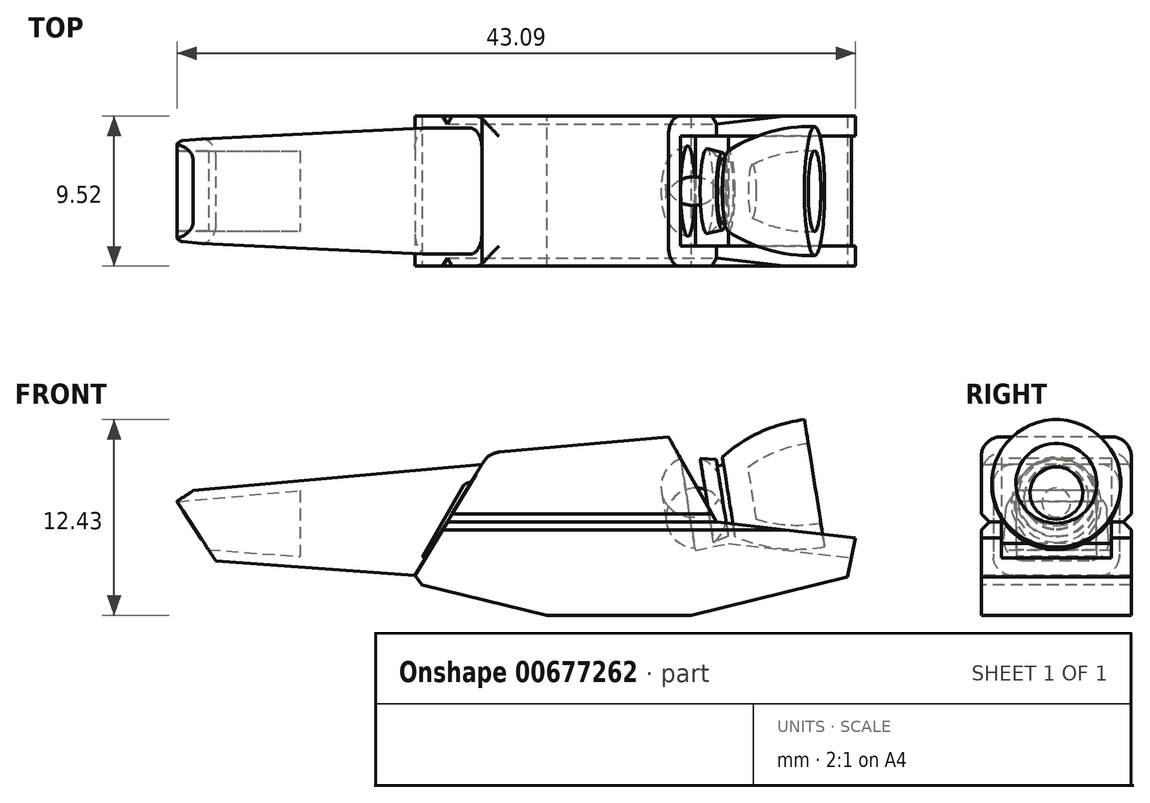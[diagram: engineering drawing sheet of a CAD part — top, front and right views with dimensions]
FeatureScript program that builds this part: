
annotation { "Feature Type Name" : "Feature", "Feature Type Description" : "" }
export const myFeature = defineFeature(function(context is Context, id is Id, definition is map)
    precondition{}
    {
        {
            var Q0;
            Q0=qCreatedBy(makeId("Front.planeOp"),FACE);
            var sketch = newSketch(context, id + "F0", { "sketchPlane" : qUnion([Q0])});
            skLineSegment(sketch, "E0", {"start": v(0, 0) * mm, "end": v(1.5, 0.24) * mm, "construction": true});
            skLineSegment(sketch, "E1", {"start": v(0, 0) * mm, "end": v(-2.23, 14.05) * mm, "construction": true});
            skLineSegment(sketch, "E2", {"start": v(5.05, 3.4) * mm, "end": v(4.82, 4.9) * mm});
            skLineSegment(sketch, "E3", {"start": v(-0.32, 2.02) * mm, "end": v(-0.4, 2.53) * mm});
            skArc(sketch, "E4", {"start": v(4.82, 4.9) * mm, "mid": v(2.02, 4.12) * mm, "end": v(-0.4, 2.53) * mm});
            skLineSegment(sketch, "E5", {"start": v(0, 0) * mm, "end": v(-19.66, -3.11) * mm, "construction": true});
            skLineSegment(sketch, "E6", {"start": v(-0.32, 2.02) * mm, "end": v(-0.72, 1.96) * mm});
            skLineSegment(sketch, "E7", {"start": v(-0.72, 1.96) * mm, "end": v(-0.79, 2.36) * mm});
            skLineSegment(sketch, "E8", {"start": v(-0.79, 2.36) * mm, "end": v(-1.8, 2.45) * mm});
            skLineSegment(sketch, "E9", {"start": v(-0.79, 2.36) * mm, "end": v(-6.83, 1.4) * mm, "construction": true});
            skLineSegment(sketch, "E10", {"start": v(-3.63, 6.1) * mm, "end": v(-2.98, 2.02) * mm, "construction": true});
            skLineSegment(sketch, "E11", {"start": v(-1.8, 2.45) * mm, "end": v(-3.02, 2.26) * mm, "construction": true});
            skPoint(sketch, "E12", {"position": v(-3.05, 2.42) * mm});
            skArc(sketch, "E13", {"start": v(-1.8, 2.45) * mm, "mid": v(-2.43, 2.54) * mm, "end": v(-3.05, 2.42) * mm});
            skLineSegment(sketch, "E14", {"start": v(-3.05, 2.42) * mm, "end": v(-2.6, -0.41) * mm});
            skLineSegment(sketch, "E15", {"start": v(-2.6, -0.41) * mm, "end": v(1.5, 0.24) * mm});
            skArc(sketch, "E16", {"start": v(5.05, 3.4) * mm, "mid": v(3.05, 2.9) * mm, "end": v(1.24, 1.9) * mm});
            skLineSegment(sketch, "E17", {"start": v(1.24, 1.9) * mm, "end": v(1.5, 0.24) * mm});
            skLineSegment(sketch, "E18.trimOffspring", {"start": v(5.46, 0.86) * mm, "end": v(24.57, 3.9) * mm, "construction": true});
            skSolve(sketch);
        }
        {
            var Q0;
            Q0=makeQuery(id+"F0.imprint","IMPRINT",FACE,{"disambiguationData":[TD([[makeQuery(id+"F0.imprint","IMPRINT",EDGE,{"derivedFrom":sQuery(id+"F0.wireOp",EDGE,"E2")}),1.0]])]});
            var Q1;
            Q1=sQuery(id+"F0.wireOp",EDGE,"E5");
            revolve(context, id + "F1", {"entities" : qUnion([Q0]), "axis" : qUnion([Q1]), "revolveType" : RevolveType.FULL});
        }
        {
            var Q0;
            Q0=qCreatedBy(makeId("Front.planeOp"),FACE);
            var sketch = newSketch(context, id + "F2", { "sketchPlane" : qUnion([Q0])});
            skLineSegment(sketch, "E19", {"start": v(0, 0) * mm, "end": v(1.56, -9.86) * mm, "construction": true});
            skLineSegment(sketch, "E20", {"start": v(0.48, -3.01) * mm, "end": v(7.8, -3.87) * mm});
            skLineSegment(sketch, "E21", {"start": v(7.8, -3.87) * mm, "end": v(7.55, -5.07) * mm});
            skLineSegment(sketch, "E22", {"start": v(7.55, -5.07) * mm, "end": v(-2.39, -7.52) * mm});
            skLineSegment(sketch, "E23", {"start": v(-2.39, -7.52) * mm, "end": v(-14.3, -6.85) * mm});
            skLineSegment(sketch, "E24", {"start": v(-19.92, -5) * mm, "end": v(-32.58, -4.06) * mm});
            skLineSegment(sketch, "E25", {"start": v(-35.04, -0.28) * mm, "end": v(-32.58, -4.06) * mm});
            skLineSegment(sketch, "E26", {"start": v(-34.01, 0.4) * mm, "end": v(-35.04, -0.28) * mm});
            skLineSegment(sketch, "E27", {"start": v(-34.01, 0.4) * mm, "end": v(-15.66, 2.07) * mm});
            skLineSegment(sketch, "E28", {"start": v(-15.66, 2.07) * mm, "end": v(-15.25, 2.78) * mm});
            skLineSegment(sketch, "E29", {"start": v(-15.25, 2.78) * mm, "end": v(-3.83, 3.82) * mm});
            skLineSegment(sketch, "E30", {"start": v(0.48, -3.01) * mm, "end": v(0, -2.95) * mm});
            skLineSegment(sketch, "E31", {"start": v(-3.83, 3.82) * mm, "end": v(-3.05, 2.44) * mm});
            skLineSegment(sketch, "E32", {"start": v(0, -2.95) * mm, "end": v(-50.8, -2.95) * mm, "construction": true});
            skLineSegment(sketch, "E33", {"start": v(-19.92, -5) * mm, "end": v(-19.48, -5.6) * mm});
            skLineSegment(sketch, "E34", {"start": v(-19.48, -5.6) * mm, "end": v(-14.3, -6.85) * mm});
            skLineSegment(sketch, "E35", {"start": v(-3.05, 2.44) * mm, "end": v(-2.12, -3.4) * mm});
            skLineSegment(sketch, "E36", {"start": v(-2.12, -3.4) * mm, "end": v(0, -2.95) * mm});
            skLineSegment(sketch, "E37", {"start": v(-2.12, -3.4) * mm, "end": v(-2.12, 15.55) * mm, "construction": true});
            skSolve(sketch);
        }
        {
            var Q0;
            Q0 = qSketchRegion(id + "F2", true);
            extrude(context, id + "F3", {"entities" : qUnion([Q0]), "operationType" : NewBodyOperationType.ADD, "endBound" : BoundingType.SYMMETRIC, "oppositeDirection" : true, "depth" : 9.52 * mm, "offsetDistance" : 25.4 * mm});
        }
        {
            var Q0;
            Q0=makeQuery(id+"F3.opExtrude","CAP_FACE",FACE,{"disambiguationData":[OSD([sQuery(id+"F2.wireOp",EDGE,"E20"),sQuery(id+"F2.wireOp",EDGE,"E21"),sQuery(id+"F2.wireOp",EDGE,"E22"),sQuery(id+"F2.wireOp",EDGE,"E23"),sQuery(id+"F2.wireOp",EDGE,"E24"),sQuery(id+"F2.wireOp",EDGE,"E25"),sQuery(id+"F2.wireOp",EDGE,"E26"),sQuery(id+"F2.wireOp",EDGE,"E27"),sQuery(id+"F2.wireOp",EDGE,"E28"),sQuery(id+"F2.wireOp",EDGE,"E29"),sQuery(id+"F2.wireOp",EDGE,"E30"),sQuery(id+"F2.wireOp",EDGE,"E31"),sQuery(id+"F2.wireOp",EDGE,"E33"),sQuery(id+"F2.wireOp",EDGE,"E34"),sQuery(id+"F2.wireOp",EDGE,"E35"),sQuery(id+"F2.wireOp",EDGE,"E36")])],"isStart":true});
            var sketch = newSketch(context, id + "F4", { "sketchPlane" : qUnion([Q0])});
            skLineSegment(sketch, "E38", {"start": v(7.8, -3.87) * mm, "end": v(8.05, -2.62) * mm});
            skLineSegment(sketch, "E39", {"start": v(8.05, -2.62) * mm, "end": v(-0.77, -1.59) * mm});
            skLineSegment(sketch, "E40", {"start": v(-3.05, 2.44) * mm, "end": v(-2.12, -3.4) * mm});
            skLineSegment(sketch, "E41", {"start": v(-2.12, -3.4) * mm, "end": v(0, -2.95) * mm});
            skLineSegment(sketch, "E42", {"start": v(0, -2.95) * mm, "end": v(7.8, -3.87) * mm});
            skLineSegment(sketch, "E43", {"start": v(-3.05, 2.44) * mm, "end": v(0, -2.95) * mm, "construction": true});
            skLineSegment(sketch, "E44", {"start": v(-3.05, 2.44) * mm, "end": v(-0.77, -1.59) * mm});
            skSolve(sketch);
        }
        {
            var Q0;
            Q0 = qSketchRegion(id + "F4", true);
            extrude(context, id + "F5", {"entities" : qUnion([Q0]), "oppositeDirection" : true, "depth" : 1.27 * mm, "offsetDistance" : 25.4 * mm});
        }
        {
            var Q0;
            Q0=makeQuery(id+"FYjz2R2zgnsnYFL_2.boolean.opBoolean","MERGE",FACE,{"derivedFrom":[makeQuery(id+"F3.opExtrude","CAP_FACE",FACE,{"disambiguationData":[OSD([sQuery(id+"F2.wireOp",EDGE,"E20"),sQuery(id+"F2.wireOp",EDGE,"E21"),sQuery(id+"F2.wireOp",EDGE,"E22"),sQuery(id+"F2.wireOp",EDGE,"E23"),sQuery(id+"F2.wireOp",EDGE,"E24"),sQuery(id+"F2.wireOp",EDGE,"E25"),sQuery(id+"F2.wireOp",EDGE,"E26"),sQuery(id+"F2.wireOp",EDGE,"E27"),sQuery(id+"F2.wireOp",EDGE,"E28"),sQuery(id+"F2.wireOp",EDGE,"E29"),sQuery(id+"F2.wireOp",EDGE,"E30"),sQuery(id+"F2.wireOp",EDGE,"E31"),sQuery(id+"F2.wireOp",EDGE,"E33"),sQuery(id+"F2.wireOp",EDGE,"E34"),sQuery(id+"F2.wireOp",EDGE,"E35"),sQuery(id+"F2.wireOp",EDGE,"E36")])],"isStart":true}),makeQuery(id+"F5.opExtrude","CAP_FACE",FACE,{"disambiguationData":[OSD([sQuery(id+"F4.wireOp",EDGE,"E38"),sQuery(id+"F4.wireOp",EDGE,"E39"),sQuery(id+"F4.wireOp",EDGE,"E40"),sQuery(id+"F4.wireOp",EDGE,"E41"),sQuery(id+"F4.wireOp",EDGE,"E42"),sQuery(id+"F4.wireOp",EDGE,"E44")])],"isStart":true})]});
            var sketch = newSketch(context, id + "F6", { "sketchPlane" : qUnion([Q0])});
            skLineSegment(sketch, "E45", {"start": v(-36.57, -5) * mm, "end": v(-36.57, 2.78) * mm});
            skLineSegment(sketch, "E46", {"start": v(-36.57, 2.78) * mm, "end": v(-15.25, 2.78) * mm});
            skLineSegment(sketch, "E47", {"start": v(-15.25, 2.78) * mm, "end": v(-19.92, -5) * mm});
            skLineSegment(sketch, "E48", {"start": v(-19.92, -5) * mm, "end": v(-36.57, -5) * mm});
            skSolve(sketch);
        }
        {
            var Q0;
            Q0 = qSketchRegion(id + "F6", true);
            extrude(context, id + "F7", {"entities" : qUnion([Q0]), "operationType" : NewBodyOperationType.REMOVE, "oppositeDirection" : true, "depth" : 0.76 * mm, "offsetDistance" : 25.4 * mm});
        }
        {
            var Q0;
            Q0=makeQuery(id+"F5.opExtrude","SWEPT_BODY",BODY,{"disambiguationData":[OSD([sQuery(id+"F4.wireOp",EDGE,"E38"),sQuery(id+"F4.wireOp",EDGE,"E39"),sQuery(id+"F4.wireOp",EDGE,"E40"),sQuery(id+"F4.wireOp",EDGE,"E41"),sQuery(id+"F4.wireOp",EDGE,"E42"),sQuery(id+"F4.wireOp",EDGE,"E44")])]});
            var Q1;
            Q1=qCreatedBy(makeId("Front.planeOp"),FACE);
            mirror(context, id + "F8", {"operationType" : NewBodyOperationType.ADD, "entities" : qUnion([Q0]), "mirrorPlane" : qUnion([Q1])});
        }
        {
            var Q0;
            Q0=makeQuery(id+"F8.boolean.opBoolean","MERGE",FACE,{"derivedFrom":[makeQuery(id+"F3.opExtrude","CAP_FACE",FACE,{"disambiguationData":[OSD([sQuery(id+"F2.wireOp",EDGE,"E20"),sQuery(id+"F2.wireOp",EDGE,"E21"),sQuery(id+"F2.wireOp",EDGE,"E22"),sQuery(id+"F2.wireOp",EDGE,"E23"),sQuery(id+"F2.wireOp",EDGE,"E24"),sQuery(id+"F2.wireOp",EDGE,"E25"),sQuery(id+"F2.wireOp",EDGE,"E26"),sQuery(id+"F2.wireOp",EDGE,"E27"),sQuery(id+"F2.wireOp",EDGE,"E28"),sQuery(id+"F2.wireOp",EDGE,"E29"),sQuery(id+"F2.wireOp",EDGE,"E30"),sQuery(id+"F2.wireOp",EDGE,"E31"),sQuery(id+"F2.wireOp",EDGE,"E33"),sQuery(id+"F2.wireOp",EDGE,"E34"),sQuery(id+"F2.wireOp",EDGE,"E35"),sQuery(id+"F2.wireOp",EDGE,"E36")])],"isStart":false}),makeQuery(id+"F8.opPattern","COPY",FACE,{"derivedFrom":makeQuery(id+"F5.opExtrude","CAP_FACE",FACE,{"disambiguationData":[OSD([sQuery(id+"F4.wireOp",EDGE,"E38"),sQuery(id+"F4.wireOp",EDGE,"E39"),sQuery(id+"F4.wireOp",EDGE,"E40"),sQuery(id+"F4.wireOp",EDGE,"E41"),sQuery(id+"F4.wireOp",EDGE,"E42"),sQuery(id+"F4.wireOp",EDGE,"E44")])],"isStart":true}),"instanceName":"1"})]});
            var sketch = newSketch(context, id + "F9", { "sketchPlane" : qUnion([Q0])});
            skLineSegment(sketch, "E49", {"start": v(15.25, 2.78) * mm, "end": v(19.92, -5) * mm});
            skLineSegment(sketch, "E50", {"start": v(19.92, -5) * mm, "end": v(36.16, -5) * mm});
            skLineSegment(sketch, "E51", {"start": v(36.16, -5) * mm, "end": v(36.16, 2.59) * mm});
            skLineSegment(sketch, "E52", {"start": v(36.16, 2.59) * mm, "end": v(15.25, 2.78) * mm});
            skSolve(sketch);
        }
        {
            var Q0;
            Q0 = qSketchRegion(id + "F9", true);
            extrude(context, id + "F10", {"entities" : qUnion([Q0]), "operationType" : NewBodyOperationType.REMOVE, "oppositeDirection" : true, "depth" : 0.76 * mm, "offsetDistance" : 25.4 * mm});
        }
        {
            var Q0;
            Q0=makeQuery(id+"F3.opExtrude","SWEPT_EDGE",EDGE,{"disambiguationData":[OSD([sQuery(id+"F2.wireOp",EDGE,"E27"),sQuery(id+"F2.wireOp",EDGE,"E28")])]});
            var Q1;
            Q1=makeQuery(id+"F3.opExtrude","SWEPT_FACE",FACE,{"disambiguationData":[OSD([sQuery(id+"F2.wireOp",EDGE,"E28")])]});
            cPlane(context, id + "F11", {"entities" : qUnion([Q0, Q1]), "cplaneType" : CPlaneType.LINE_ANGLE, "offset" : 25.4 * mm, "angle" : 90 * degree, "width" : 152.4 * mm, "height" : 152.4 * mm});
        }
        {
            var Q0;
            Q0=qCreatedBy(id+"F11.planeOp",FACE);
            var sketch = newSketch(context, id + "F12", { "sketchPlane" : qUnion([Q0])});
            skLineSegment(sketch, "E53", {"start": v(-14.89, -7.16) * mm, "end": v(-14.89, 7.16) * mm, "construction": true});
            skLineSegment(sketch, "E54", {"start": v(0, 0) * mm, "end": v(-46.94, 0) * mm, "construction": true});
            skLineSegment(sketch, "E55", {"start": v(-30.26, -3.18) * mm, "end": v(-30.26, 3.18) * mm, "construction": true});
            skLineSegment(sketch, "E56", {"start": v(-30.26, -3.18) * mm, "end": v(-14.89, -4) * mm});
            skLineSegment(sketch, "E57", {"start": v(-14.89, -4) * mm, "end": v(-30.26, -4.28) * mm});
            skLineSegment(sketch, "E58", {"start": v(-30.26, -4.28) * mm, "end": v(-30.26, -3.18) * mm});
            skLineSegment(sketch, "E59.MirrorCS", {"start": v(-14.89, 4) * mm, "end": v(-30.26, 4.28) * mm});
            skLineSegment(sketch, "E60.MirrorCS", {"start": v(-30.26, 3.18) * mm, "end": v(-14.89, 4) * mm});
            skLineSegment(sketch, "E61.MirrorCS", {"start": v(-30.26, 4.28) * mm, "end": v(-30.26, 3.18) * mm});
            skSolve(sketch);
        }
        {
            var Q0;
            Q0 = qSketchRegion(id + "F12", true);
            extrude(context, id + "F13", {"entities" : qUnion([Q0]), "operationType" : NewBodyOperationType.REMOVE, "endBound" : BoundingType.THROUGH_ALL, "oppositeDirection" : true, "depth" : 25.4 * mm, "offsetDistance" : 25.4 * mm});
        }
        {
            var Q0;
            Q0=qCreatedBy(makeId("Front.planeOp"),FACE);
            var sketch = newSketch(context, id + "F14", { "sketchPlane" : qUnion([Q0])});
            skLineSegment(sketch, "E62", {"start": v(-35.68, -0.37) * mm, "end": v(-27.21, 0.4) * mm});
            skLineSegment(sketch, "E63", {"start": v(0.5, 0) * mm, "end": v(-37.1, 0) * mm, "construction": true});
            skLineSegment(sketch, "E64", {"start": v(-33.95, -3.29) * mm, "end": v(-27.21, -3.79) * mm});
            skLineSegment(sketch, "E65", {"start": v(-33.95, -3.29) * mm, "end": v(-35.68, -0.37) * mm});
            skLineSegment(sketch, "E66", {"start": v(-27.21, 0.4) * mm, "end": v(-27.21, -3.79) * mm});
            skPoint(sketch, "E67.orphan", {"position": v(-19.1, 1.14) * mm});
            skSolve(sketch);
        }
        {
            var Q0;
            Q0 = qSketchRegion(id + "F14", true);
            extrude(context, id + "F15", {"entities" : qUnion([Q0]), "operationType" : NewBodyOperationType.REMOVE, "endBound" : BoundingType.SYMMETRIC, "oppositeDirection" : true, "depth" : 5.08 * mm, "offsetDistance" : 25.4 * mm});
        }
        {
            var Q0;
            Q0=qCreatedBy(makeId("Right.planeOp"),FACE);
            var sketch = newSketch(context, id + "F16", { "sketchPlane" : qUnion([Q0])});
            skLineSegment(sketch, "E68", {"start": v(-5.3, -1.59) * mm, "end": v(-3.08, -1.59) * mm, "construction": true});
            skLineSegment(sketch, "E69", {"start": v(-4.76, -1.53) * mm, "end": v(-4.76, -1.65) * mm, "construction": true});
            skLineSegment(sketch, "E70", {"start": v(-4.25, -1.59) * mm, "end": v(-4.82, -1.02) * mm});
            skLineSegment(sketch, "E71", {"start": v(-4.82, -1.02) * mm, "end": v(-4.82, -1.59) * mm});
            skLineSegment(sketch, "E72.MirrorCS", {"start": v(-4.82, -2.15) * mm, "end": v(-4.82, -1.59) * mm});
            skLineSegment(sketch, "E73.MirrorCS", {"start": v(-4.25, -1.59) * mm, "end": v(-4.82, -2.15) * mm});
            skLineSegment(sketch, "E74", {"start": v(0, 0) * mm, "end": v(0, -3.64) * mm, "construction": true});
            skLineSegment(sketch, "E75.MirrorCS", {"start": v(4.82, -1.02) * mm, "end": v(4.82, -1.59) * mm});
            skLineSegment(sketch, "E76.MirrorCS", {"start": v(4.82, -2.15) * mm, "end": v(4.82, -1.59) * mm});
            skLineSegment(sketch, "E77.MirrorCS", {"start": v(4.25, -1.59) * mm, "end": v(4.82, -2.15) * mm});
            skLineSegment(sketch, "E78.MirrorCS", {"start": v(4.25, -1.59) * mm, "end": v(4.82, -1.02) * mm});
            skSolve(sketch);
        }
        {
            var Q0;
            Q0 = qSketchRegion(id + "F16", true);
            extrude(context, id + "F17", {"entities" : qUnion([Q0]), "operationType" : NewBodyOperationType.REMOVE, "endBound" : BoundingType.SYMMETRIC, "oppositeDirection" : true, "depth" : 50.8 * mm, "offsetDistance" : 25.4 * mm});
        }
        {
            var Q0;
            Q0=makeQuery(id+"F13.boolean.opBoolean","INTERSECT",EDGE,{"derivedFrom":[makeQuery(id+"F3.opExtrude","SWEPT_FACE",FACE,{"disambiguationData":[OSD([sQuery(id+"F2.wireOp",EDGE,"E27")])]}),makeQuery(id+"F13.opExtrude","SWEPT_FACE",FACE,{"disambiguationData":[OSD([sQuery(id+"F12.wireOp",EDGE,"E56")])]})]});
            var Q1;
            Q1=makeQuery(id+"F13.boolean.opBoolean","INTERSECT",EDGE,{"derivedFrom":[makeQuery(id+"F3.opExtrude","SWEPT_FACE",FACE,{"disambiguationData":[OSD([sQuery(id+"F2.wireOp",EDGE,"E27")])]}),makeQuery(id+"F13.opExtrude","SWEPT_FACE",FACE,{"disambiguationData":[OSD([sQuery(id+"F12.wireOp",EDGE,"E60.MirrorCS")])]})]});
            var Q2;
            Q2=makeQuery(id+"F13.boolean.opBoolean","INTERSECT",EDGE,{"derivedFrom":[makeQuery(id+"F3.opExtrude","SWEPT_FACE",FACE,{"disambiguationData":[OSD([sQuery(id+"F2.wireOp",EDGE,"E24")])]}),makeQuery(id+"F13.opExtrude","SWEPT_FACE",FACE,{"disambiguationData":[OSD([sQuery(id+"F12.wireOp",EDGE,"E56")])]})]});
            var Q3;
            Q3=makeQuery(id+"F13.boolean.opBoolean","INTERSECT",EDGE,{"derivedFrom":[makeQuery(id+"F3.opExtrude","SWEPT_FACE",FACE,{"disambiguationData":[OSD([sQuery(id+"F2.wireOp",EDGE,"E24")])]}),makeQuery(id+"F13.opExtrude","SWEPT_FACE",FACE,{"disambiguationData":[OSD([sQuery(id+"F12.wireOp",EDGE,"E60.MirrorCS")])]})]});
            var Q4;
            Q4=makeQuery(id+"F3.opExtrude","CAP_EDGE",EDGE,{"disambiguationData":[OSD([sQuery(id+"F2.wireOp",EDGE,"E29")])],"isStart":true});
            var Q5;
            Q5=makeQuery(id+"F3.opExtrude","CAP_EDGE",EDGE,{"disambiguationData":[OSD([sQuery(id+"F2.wireOp",EDGE,"E29")])],"isStart":false});
            var Q6;
            Q6=makeQuery(id+"F3.opExtrude","SWEPT_EDGE",EDGE,{"disambiguationData":[OSD([sQuery(id+"F2.wireOp",EDGE,"E28"),sQuery(id+"F2.wireOp",EDGE,"E29")])]});
            fillet(context, id + "F18", {"entities" : qUnion([Q0, Q1, Q2, Q3, Q4, Q5, Q6]), "radius" : 1.27 * mm, "tangentPropagation" : true, "allowEdgeOverflow" : false});
        }
        {
            var Q0;
            Q0=qCreatedBy(makeId("Front.planeOp"),FACE);
            var sketch = newSketch(context, id + "F19", { "sketchPlane" : qUnion([Q0])});
            skLineSegment(sketch, "E79", {"start": v(-14.3, -6.85) * mm, "end": v(-11.53, -7.52) * mm});
            skLineSegment(sketch, "E80", {"start": v(-11.53, -7.52) * mm, "end": v(-2.39, -7.52) * mm});
            skLineSegment(sketch, "E81", {"start": v(-14.3, -6.85) * mm, "end": v(-2.39, -7.52) * mm});
            skSolve(sketch);
        }
        {
            var Q0;
            Q0 = qSketchRegion(id + "F19", true);
            extrude(context, id + "F20", {"entities" : qUnion([Q0]), "operationType" : NewBodyOperationType.ADD, "endBound" : BoundingType.SYMMETRIC, "depth" : 9.52 * mm, "offsetDistance" : 25.4 * mm});
        }
    });
